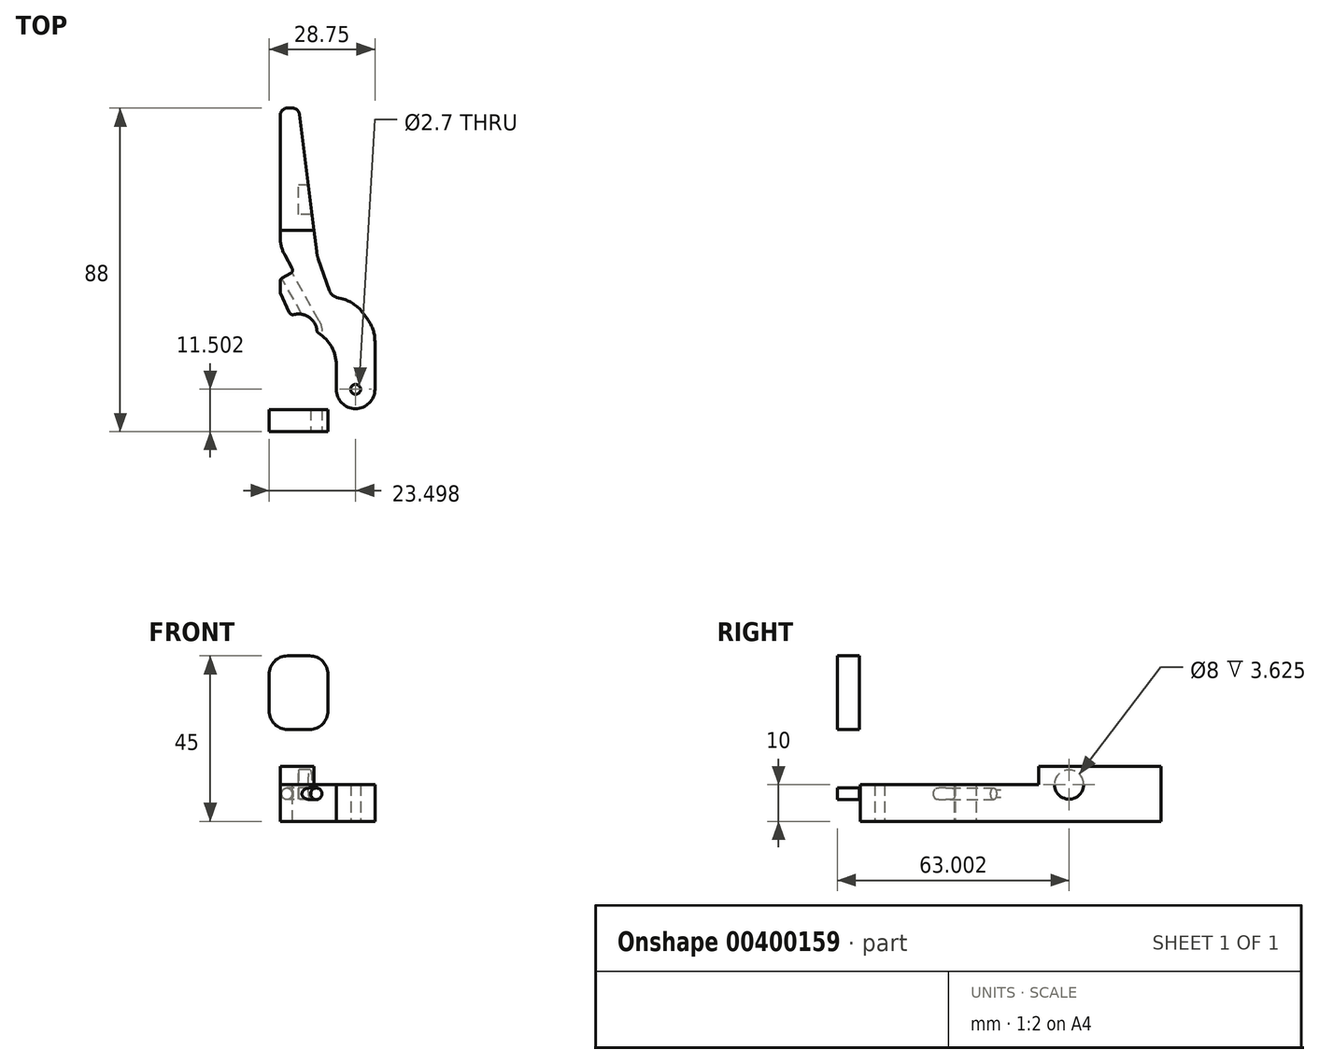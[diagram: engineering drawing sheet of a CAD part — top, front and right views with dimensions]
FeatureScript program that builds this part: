
annotation { "Feature Type Name" : "Feature", "Feature Type Description" : "" }
export const myFeature = defineFeature(function(context is Context, id is Id, definition is map)
    precondition{}
    {
        {
            var Q0;
            Q0=qCreatedBy(makeId("Top.planeOp"),FACE);
            var sketch = newSketch(context, id + "F0", { "sketchPlane" : qUnion([Q0])});
            skLineSegment(sketch, "E0", {"start": v(-10.82, 50.62) * mm, "end": v(-10.82, 5.62) * mm});
            skCircle(sketch, "E1.MirrorC", {"center": v(-0.32, 45.12) * mm, "radius": 1.75 * mm});
            skCircle(sketch, "E2.MirrorC", {"center": v(-0.32, 14.12) * mm, "radius": 1.75 * mm});
            skCircle(sketch, "E3.MirrorC", {"center": v(30.68, 45.12) * mm, "radius": 1.75 * mm});
            skLineSegment(sketch, "E4.MirrorCS", {"start": v(46.18, 90.62) * mm, "end": v(41.18, 90.62) * mm});
            skLineSegment(sketch, "E5.MirrorCS", {"start": v(41.18, 90.62) * mm, "end": v(36.18, 50.62) * mm});
            skLineSegment(sketch, "E6.MirrorCS", {"start": v(36.18, 50.62) * mm, "end": v(30.68, 50.62) * mm});
            skLineSegment(sketch, "E7.MirrorCS", {"start": v(36.18, 8.62) * mm, "end": v(-5.82, 8.62) * mm});
            skLineSegment(sketch, "E8.MirrorCS", {"start": v(36.18, 50.62) * mm, "end": v(36.18, 8.62) * mm});
            skLineSegment(sketch, "E9.MirrorCS", {"start": v(-5.82, 50.62) * mm, "end": v(-5.82, 8.62) * mm});
            skArc(sketch, "E10.MirrorC", {"start": v(-0.32, 50.62) * mm, "mid": v(3.57, 49.01) * mm, "end": v(5.18, 45.12) * mm});
            skLineSegment(sketch, "E11.MirrorCS", {"start": v(46.18, 5.62) * mm, "end": v(46.18, 90.62) * mm});
            skLineSegment(sketch, "E12.MirrorCS", {"start": v(-10.82, 5.62) * mm, "end": v(46.18, 5.62) * mm});
            skLineSegment(sketch, "E13", {"start": v(-5.82, 50.62) * mm, "end": v(-10.82, 50.62) * mm});
            skLineSegment(sketch, "E14", {"start": v(5.18, 45.12) * mm, "end": v(5.18, 35.3) * mm});
            skLineSegment(sketch, "E15", {"start": v(-5.82, 8.62) * mm, "end": v(-5.82, 5.62) * mm});
            skLineSegment(sketch, "E16", {"start": v(36.18, 8.62) * mm, "end": v(36.18, 5.62) * mm});
            skArc(sketch, "E17", {"start": v(5.18, 35.3) * mm, "mid": v(3.68, 29.62) * mm, "end": v(5.18, 23.94) * mm});
            skArc(sketch, "E18", {"start": v(5.18, 23.94) * mm, "mid": v(9.4, 19.68) * mm, "end": v(15.18, 18.12) * mm});
            skLineSegment(sketch, "E19", {"start": v(15.18, 18.12) * mm, "end": v(23.18, 18.12) * mm});
            skPoint(sketch, "E20.end.orphan", {"position": v(15.18, 8.62) * mm});
            skLineSegment(sketch, "E21", {"start": v(23.18, 18.12) * mm, "end": v(23.18, 8.62) * mm});
            skPoint(sketch, "E22.trimOffspring.end.orphan", {"position": v(23.18, 0) * mm});
            skCircle(sketch, "E23", {"center": v(30.68, 14.12) * mm, "radius": 1.35 * mm});
            skLineSegment(sketch, "E24.trimOffspring", {"start": v(-0.32, 50.62) * mm, "end": v(-5.82, 50.62) * mm});
            skLineSegment(sketch, "E25", {"start": v(10.18, 65.16) * mm, "end": v(10.18, 52.87) * mm});
            skLineSegment(sketch, "E26", {"start": v(10.18, 65.16) * mm, "end": v(10.18, 90.62) * mm});
            skLineSegment(sketch, "E27", {"start": v(10.18, 90.62) * mm, "end": v(15.18, 90.62) * mm});
            skLineSegment(sketch, "E28", {"start": v(15.18, 90.62) * mm, "end": v(20.18, 50.62) * mm});
            skCircle(sketch, "E29", {"center": v(15.18, 29.62) * mm, "radius": 4 * mm});
            skArc(sketch, "E30", {"start": v(30.68, 50.62) * mm, "mid": v(25.18, 45.12) * mm, "end": v(30.68, 39.62) * mm});
            skLineSegment(sketch, "E31", {"start": v(30.68, 39.62) * mm, "end": v(36.18, 39.62) * mm});
            skLineSegment(sketch, "E32", {"start": v(10.18, 42.2) * mm, "end": v(10.18, 40.62) * mm});
            skLineSegment(sketch, "E33", {"start": v(27.5, 38.6) * mm, "end": v(30.68, 37.71) * mm});
            skLineSegment(sketch, "E34", {"start": v(10.18, 40.35) * mm, "end": v(12.75, 34.83) * mm});
            skLineSegment(sketch, "E35", {"start": v(10.18, 40.62) * mm, "end": v(10.18, 40.35) * mm});
            skArc(sketch, "E36", {"start": v(25.43, 14.12) * mm, "mid": v(30.68, 8.87) * mm, "end": v(35.93, 14.12) * mm});
            skLineSegment(sketch, "E37", {"start": v(25.43, 14.12) * mm, "end": v(25.43, 29.62) * mm});
            skLineSegment(sketch, "E38", {"start": v(35.93, 14.12) * mm, "end": v(35.93, 30.4) * mm});
            skLineSegment(sketch, "E39", {"start": v(30.68, 37.71) * mm, "end": v(35.93, 30.4) * mm});
            skLineSegment(sketch, "E40", {"start": v(11.37, 37.8) * mm, "end": v(9.16, 36.55) * mm});
            skPoint(sketch, "E41", {"position": v(12.24, 44.65) * mm});
            skLineSegment(sketch, "E42.trimOffspring", {"start": v(14.96, 39.81) * mm, "end": v(19.36, 31.97) * mm});
            skArc(sketch, "E43", {"start": v(19.98, 29.62) * mm, "mid": v(19.82, 30.84) * mm, "end": v(19.36, 31.97) * mm});
            skArc(sketch, "E44", {"start": v(20.18, 29.62) * mm, "mid": v(17.87, 33.84) * mm, "end": v(13.07, 34.15) * mm});
            skLineSegment(sketch, "E45", {"start": v(25.43, 29.62) * mm, "end": v(20.18, 29.62) * mm});
            skLineSegment(sketch, "E46", {"start": v(12.75, 34.83) * mm, "end": v(13.07, 34.15) * mm});
            skLineSegment(sketch, "E47.trimOffspring", {"start": v(10.18, 44.1) * mm, "end": v(10.18, 42.2) * mm});
            skLineSegment(sketch, "E48", {"start": v(10.18, 44.1) * mm, "end": v(13.93, 46.2) * mm});
            skLineSegment(sketch, "E49", {"start": v(13.93, 46.2) * mm, "end": v(10.18, 52.87) * mm});
            skPoint(sketch, "E50.start.orphan", {"position": v(12.24, 45.94) * mm});
            skLineSegment(sketch, "E51", {"start": v(27.5, 38.6) * mm, "end": v(25.54, 39.13) * mm});
            skLineSegment(sketch, "E52", {"start": v(20.18, 50.62) * mm, "end": v(23.51, 41.04) * mm});
            skPoint(sketch, "E53.visualSharp", {"position": v(24.03, 39.55) * mm});
            skArc(sketch, "E53.filletArc", {"start": v(23.51, 41.04) * mm, "mid": v(24.3, 39.84) * mm, "end": v(25.54, 39.13) * mm});
            skLineSegment(sketch, "E54", {"start": v(10.18, 57.39) * mm, "end": v(19.33, 57.39) * mm});
            skSolve(sketch);
        }
        {
            var Q0;
            Q0=makeQuery(id+"F0.imprint","IMPRINT",FACE,{"disambiguationData":[TD([[makeQuery(id+"F0.imprint","IMPRINT",EDGE,{"derivedFrom":sQuery(id+"F0.wireOp",EDGE,"E1.MirrorC")}),1.0]])]});
            var Q1;
            Q1=makeQuery(id+"F0.imprint","IMPRINT",FACE,{"disambiguationData":[TD([[makeQuery(id+"F0.imprint","IMPRINT",EDGE,{"derivedFrom":sQuery(id+"F0.wireOp",EDGE,"E3.MirrorC")}),1.0]])]});
            var Q2;
            Q2=makeQuery(id+"F0.imprint","IMPRINT",FACE,{"disambiguationData":[TD([[makeQuery(id+"F0.imprint","IMPRINT",EDGE,{"derivedFrom":sQuery(id+"F0.wireOp",EDGE,"E0")}),1.0]])]});
            var Q3;
            Q3=makeQuery(id+"F0.imprint","IMPRINT",FACE,{"disambiguationData":[TD([[makeQuery(id+"F0.imprint","IMPRINT",EDGE,{"derivedFrom":sQuery(id+"F0.wireOp",EDGE,"E4.MirrorCS")}),1.0]])]});
            var Q4;
            {var subQ0=sQuery(id+"F0.wireOp",EDGE,"E15");Q4=makeQuery(id+"F0.imprint","IMPRINT",FACE,{"disambiguationData":[TD([[makeQuery(id+"F0.imprint","IMPRINT",EDGE,{"derivedFrom":subQ0}),1.0]])]});}
            extrude(context, id + "F1", {"entities" : qUnion([Q0, Q1, Q2, Q3, Q4]), "depth" : 5 * mm});
        }
        {
            var Q0;
            {var subQ1=sQuery(id+"F0.wireOp",EDGE,"E0");Q0=makeQuery(id+"F0.imprint","IMPRINT",FACE,{"disambiguationData":[TD([[makeQuery(id+"F0.imprint","IMPRINT",EDGE,{"derivedFrom":subQ1}),1.0]])]});}
            var Q1;
            {var subQ0=sQuery(id+"F0.wireOp",EDGE,"E15");Q1=makeQuery(id+"F0.imprint","IMPRINT",FACE,{"disambiguationData":[TD([[makeQuery(id+"F0.imprint","IMPRINT",EDGE,{"derivedFrom":subQ0}),1.0]])]});}
            var Q2;
            Q2=makeQuery(id+"F0.imprint","IMPRINT",FACE,{"disambiguationData":[TD([[makeQuery(id+"F0.imprint","IMPRINT",EDGE,{"derivedFrom":sQuery(id+"F0.wireOp",EDGE,"E4.MirrorCS")}),1.0]])]});
            extrude(context, id + "F2", {"entities" : qUnion([Q0, Q1, Q2]), "operationType" : NewBodyOperationType.ADD, "depth" : 10 * mm});
        }
        {
            var Q0;
            {var subQ0=sQuery(id+"F0.wireOp",EDGE,"E15");Q0=makeQuery(id+"F0.imprint","IMPRINT",FACE,{"disambiguationData":[TD([[makeQuery(id+"F0.imprint","IMPRINT",EDGE,{"derivedFrom":subQ0}),1.0]])]});}
            extrude(context, id + "F3", {"entities" : qUnion([Q0]), "operationType" : NewBodyOperationType.ADD, "depth" : 20 * mm});
        }
        {
            var Q0;
            Q0=makeQuery(id+"F3.opExtrude","CAP_FACE",FACE,{"disambiguationData":[OSD([sQuery(id+"F0.wireOp",EDGE,"E7.MirrorCS"),sQuery(id+"F0.wireOp",EDGE,"E12.MirrorCS"),sQuery(id+"F0.wireOp",EDGE,"E15"),sQuery(id+"F0.wireOp",EDGE,"E16")])],"isStart":false});
            var sketch = newSketch(context, id + "F4", { "sketchPlane" : qUnion([Q0])});
            skLineSegment(sketch, "E55.bottom", {"start": v(7.18, 8.62) * mm, "end": v(23.18, 8.62) * mm});
            skLineSegment(sketch, "E55.top", {"start": v(7.18, 5.62) * mm, "end": v(23.18, 5.62) * mm});
            skLineSegment(sketch, "E55.left", {"start": v(7.18, 8.62) * mm, "end": v(7.18, 5.62) * mm});
            skLineSegment(sketch, "E55.right", {"start": v(23.18, 8.62) * mm, "end": v(23.18, 5.62) * mm});
            skSolve(sketch);
        }
        {
            var Q0;
            Q0=makeQuery(id+"F2.opExtrude","SWEPT_EDGE",EDGE,{"disambiguationData":[OSD([sQuery(id+"F0.wireOp",EDGE,"E7.MirrorCS"),sQuery(id+"F0.wireOp",EDGE,"E9.MirrorCS"),sQuery(id+"F0.wireOp",EDGE,"E15")])]});
            var Q1;
            Q1=makeQuery(id+"F2.opExtrude","SWEPT_EDGE",EDGE,{"disambiguationData":[OSD([sQuery(id+"F0.wireOp",EDGE,"E7.MirrorCS"),sQuery(id+"F0.wireOp",EDGE,"E8.MirrorCS"),sQuery(id+"F0.wireOp",EDGE,"E16")])]});
            chamfer(context, id + "F5", {"entities" : qUnion([Q0, Q1]), "width" : 3.5 * mm, "tangentPropagation" : true});
        }
        {
            var Q0;
            {var subQ0=sQuery(id+"F0.wireOp",EDGE,"E11.MirrorCS");Q0=makeQuery(id+"F2.boolean.opBoolean","MERGE",FACE,{"derivedFrom":[makeQuery(id+"F1.opExtrude","SWEPT_FACE",FACE,{"disambiguationData":[OSD([subQ0])]}),makeQuery(id+"F2.opExtrude","SWEPT_FACE",FACE,{"disambiguationData":[OSD([subQ0])]})]});}
            var sketch = newSketch(context, id + "F6", { "sketchPlane" : qUnion([Q0])});
            skCircle(sketch, "E56", {"center": v(65.62, 5) * mm, "radius": 4 * mm});
            skCircle(sketch, "E57.cCircle", {"center": v(65.62, 5) * mm, "radius": 2.75 * mm, "construction": true});
            skLineSegment(sketch, "E57.0", {"start": v(62.87, 3.41) * mm, "end": v(62.87, 6.59) * mm});
            skLineSegment(sketch, "E57.1", {"start": v(62.87, 6.59) * mm, "end": v(65.62, 8.18) * mm});
            skLineSegment(sketch, "E57.2", {"start": v(65.62, 8.18) * mm, "end": v(68.37, 6.59) * mm});
            skLineSegment(sketch, "E57.3", {"start": v(68.37, 6.59) * mm, "end": v(68.37, 3.41) * mm});
            skLineSegment(sketch, "E57.4", {"start": v(68.37, 3.41) * mm, "end": v(65.62, 1.82) * mm});
            skLineSegment(sketch, "E57.5", {"start": v(65.62, 1.82) * mm, "end": v(62.87, 3.41) * mm});
            skPoint(sketch, "E57.0.midPoint", {"position": v(62.87, 5) * mm});
            skCircle(sketch, "E58", {"center": v(65.62, 5) * mm, "radius": 1.6 * mm});
            skSolve(sketch);
        }
        {
            var Q0;
            Q0=makeQuery(id+"F6.imprint","IMPRINT",FACE,{"disambiguationData":[TD([[makeQuery(id+"F6.imprint","IMPRINT",EDGE,{"derivedFrom":sQuery(id+"F6.wireOp",EDGE,"E56")}),1.0]])]});
            extrude(context, id + "F7", {"entities" : qUnion([Q0]), "operationType" : NewBodyOperationType.REMOVE, "oppositeDirection" : true, "depth" : 25 * mm});
        }
        {
            var Q0;
            Q0=makeQuery(id+"F6.imprint","IMPRINT",FACE,{"disambiguationData":[TD([[makeQuery(id+"F6.imprint","IMPRINT",EDGE,{"derivedFrom":sQuery(id+"F6.wireOp",EDGE,"E56")}),1.0]])]});
            extrude(context, id + "F8", {"entities" : qUnion([Q0]), "operationType" : NewBodyOperationType.ADD, "oppositeDirection" : true, "depth" : 6.5 * mm});
        }
        {
            var Q0;
            Q0=makeQuery(id+"F6.imprint","IMPRINT",FACE,{"disambiguationData":[TD([[makeQuery(id+"F6.imprint","IMPRINT",EDGE,{"derivedFrom":sQuery(id+"F6.wireOp",EDGE,"E57.0")}),-1.0]])]});
            extrude(context, id + "F9", {"entities" : qUnion([Q0]), "operationType" : NewBodyOperationType.REMOVE, "oppositeDirection" : true, "depth" : 25 * mm});
        }
        {
            var Q0;
            Q0=makeQuery(id+"F6.imprint","IMPRINT",FACE,{"disambiguationData":[TD([[makeQuery(id+"F6.imprint","IMPRINT",EDGE,{"derivedFrom":sQuery(id+"F6.wireOp",EDGE,"E57.0")}),-1.0]])]});
            extrude(context, id + "F10", {"entities" : qUnion([Q0]), "operationType" : NewBodyOperationType.ADD, "oppositeDirection" : true, "depth" : 4 * mm});
        }
        {
            var Q0;
            Q0=makeQuery(id+"F6.imprint","IMPRINT",FACE,{"disambiguationData":[TD([[makeQuery(id+"F6.imprint","IMPRINT",EDGE,{"derivedFrom":sQuery(id+"F6.wireOp",EDGE,"E58")}),1.0]])]});
            extrude(context, id + "F11", {"entities" : qUnion([Q0]), "operationType" : NewBodyOperationType.REMOVE, "oppositeDirection" : true, "depth" : 25 * mm});
        }
        {
            var Q0;
            {var subQ0=sQuery(id+"F0.wireOp",EDGE,"E12.MirrorCS");Q0=makeQuery(id+"F16.boolean.opBoolean","MERGE",FACE,{"derivedFrom":[makeQuery(id+"F3.boolean.opBoolean","MERGE",FACE,{"derivedFrom":[makeQuery(id+"F2.boolean.opBoolean","MERGE",FACE,{"derivedFrom":[makeQuery(id+"F1.opExtrude","SWEPT_FACE",FACE,{"disambiguationData":[OSD([subQ0])]}),makeQuery(id+"F2.opExtrude","SWEPT_FACE",FACE,{"disambiguationData":[OSD([subQ0])]})]}),makeQuery(id+"F3.opExtrude","SWEPT_FACE",FACE,{"disambiguationData":[OSD([subQ0])]})]}),makeQuery(id+"F16.opExtrude","SWEPT_FACE",FACE,{"disambiguationData":[OSD([sQuery(id+"F4.wireOp",EDGE,"E55.top")])]})]});}
            var sketch = newSketch(context, id + "F12", { "sketchPlane" : qUnion([Q0])});
            skLineSegment(sketch, "E59", {"start": v(-10.82, 2.5) * mm, "end": v(46.18, 2.5) * mm});
            skCircle(sketch, "E60", {"center": v(19.98, 2.5) * mm, "radius": 1.55 * mm});
            skSolve(sketch);
        }
        {
            var Q0;
            {var subQ0=sQuery(id+"F12.wireOp",EDGE,"E60");var subQ1=sQuery(id+"F12.wireOp",EDGE,"E59");var subQ2=makeQuery(id+"F12.imprint","INTERSECT",VERTEX,{"disambiguationData":[OD(0.0)],"derivedFrom":[subQ1,subQ0]});Q0=makeQuery(id+"F12.imprint","IMPRINT",FACE,{"disambiguationData":[TD([[makeQuery(id+"F12.imprint","IMPRINT",EDGE,{"disambiguationData":[TD([[subQ2,-1.0]])],"derivedFrom":subQ1}),1.0]])]});}
            var Q1;
            {var subQ0=sQuery(id+"F12.wireOp",EDGE,"E60");var subQ1=sQuery(id+"F12.wireOp",EDGE,"E59");var subQ2=makeQuery(id+"F12.imprint","INTERSECT",VERTEX,{"disambiguationData":[OD(0.0)],"derivedFrom":[subQ1,subQ0]});Q1=makeQuery(id+"F12.imprint","IMPRINT",FACE,{"disambiguationData":[TD([[makeQuery(id+"F12.imprint","IMPRINT",EDGE,{"disambiguationData":[TD([[subQ2,-1.0]])],"derivedFrom":subQ1}),-1.0]])]});}
            extrude(context, id + "F13", {"entities" : qUnion([Q0, Q1]), "operationType" : NewBodyOperationType.REMOVE, "endBound" : BoundingType.THROUGH_ALL, "oppositeDirection" : true, "depth" : 25 * mm});
        }
        {
            var Q0;
            Q0=makeQuery(id+"F0.imprint","IMPRINT",FACE,{"disambiguationData":[TD([[makeQuery(id+"F0.imprint","IMPRINT",EDGE,{"derivedFrom":sQuery(id+"F0.wireOp",EDGE,"E23")}),-1.0]])]});
            var Q1;
            Q1=makeQuery(id+"F0.imprint","IMPRINT",FACE,{"disambiguationData":[TD([[makeQuery(id+"F0.imprint","IMPRINT",EDGE,{"derivedFrom":sQuery(id+"F0.wireOp",EDGE,"E25")}),1.0]])]});
            extrude(context, id + "F14", {"entities" : qUnion([Q0, Q1]), "depth" : 5 * mm});
        }
        {
            var Q0;
            Q0=makeQuery(id+"F14.opExtrude","SWEPT_FACE",FACE,{"disambiguationData":[OSD([sQuery(id+"F0.wireOp",EDGE,"E45")])]});
            var sketch = newSketch(context, id + "F15", { "sketchPlane" : qUnion([Q0])});
            skCircle(sketch, "E61", {"center": v(19.98, 2.5) * mm, "radius": 1.6 * mm});
            skSolve(sketch);
        }
        {
            var Q0;
            Q0=makeQuery(id+"F4.imprint","IMPRINT",FACE,{"disambiguationData":[TD([[makeQuery(id+"F4.imprint","IMPRINT",EDGE,{"derivedFrom":sQuery(id+"F4.wireOp",EDGE,"E55.bottom")}),1.0]])]});
            extrude(context, id + "F16", {"entities" : qUnion([Q0]), "operationType" : NewBodyOperationType.ADD, "depth" : 20 * mm});
        }
        {
            var Q0;
            {var subQ0=sQuery(id+"F15.wireOp",EDGE,"E61");var subQ1=makeQuery(id+"F14.opExtrude","SWEPT_EDGE",EDGE,{"disambiguationData":[OSD([sQuery(id+"F0.wireOp",EDGE,"E44"),sQuery(id+"F0.wireOp",EDGE,"E45")])]});var subQ2=makeQuery(id+"F15.imprint","INTERSECT",VERTEX,{"disambiguationData":[OD(0.0)],"derivedFrom":[subQ1,subQ0]});Q0=makeQuery(id+"F15.imprint","IMPRINT",FACE,{"disambiguationData":[TD([[makeQuery(id+"F15.imprint","IMPRINT",EDGE,{"disambiguationData":[TD([[subQ2,-1.0]])],"derivedFrom":subQ0}),1.0]])]});}
            var Q1;
            {var subQ0=sQuery(id+"F15.wireOp",EDGE,"E61");var subQ1=makeQuery(id+"F14.opExtrude","SWEPT_EDGE",EDGE,{"disambiguationData":[OSD([sQuery(id+"F0.wireOp",EDGE,"E44"),sQuery(id+"F0.wireOp",EDGE,"E45")])]});var subQ2=makeQuery(id+"F15.imprint","INTERSECT",VERTEX,{"disambiguationData":[OD(0.0)],"derivedFrom":[subQ1,subQ0]});Q1=makeQuery(id+"F15.imprint","IMPRINT",FACE,{"disambiguationData":[TD([[makeQuery(id+"F15.imprint","IMPRINT",EDGE,{"disambiguationData":[TD([[subQ2,1.0]])],"derivedFrom":subQ0}),1.0]])]});}
            var Q2;
            Q2=sQuery(id+"F0.wireOp",EDGE,"E43");
            var Q3;
            Q3=sQuery(id+"F0.wireOp",EDGE,"E42.trimOffspring");
            sweep(context, id + "F17", {"operationType" : NewBodyOperationType.REMOVE, "profiles" : qUnion([Q0, Q1]), "path" : qUnion([Q2, Q3])});
        }
        {
            var Q0;
            Q0=sQuery(id+"F0.wireOp",EDGE,"E40");
            cPlane(context, id + "F18", {"entities" : qUnion([Q0]), "cplaneType" : CPlaneType.LINE_ANGLE, "offset" : 25 * mm, "angle" : 0 * degree, "width" : 150 * mm, "height" : 150 * mm});
        }
        {
            var Q0;
            Q0=qCreatedBy(id+"F18.planeOp",FACE);
            var sketch = newSketch(context, id + "F19", { "sketchPlane" : qUnion([Q0])});
            skCircle(sketch, "E62", {"center": v(32.55, 2.5) * mm, "radius": 1.6 * mm});
            skSolve(sketch);
        }
        {
            var Q0;
            Q0 = qSketchRegion(id + "F19", true);
            extrude(context, id + "F20", {"entities" : qUnion([Q0]), "operationType" : NewBodyOperationType.REMOVE, "oppositeDirection" : true, "depth" : 25 * mm});
        }
        {
            var Q0;
            Q0=makeQuery(id+"F0.imprint","IMPRINT",FACE,{"disambiguationData":[TD([[makeQuery(id+"F0.imprint","IMPRINT",EDGE,{"derivedFrom":sQuery(id+"F0.wireOp",EDGE,"E25")}),1.0]])]});
            extrude(context, id + "F21", {"entities" : qUnion([Q0]), "operationType" : NewBodyOperationType.ADD, "depth" : 10 * mm});
        }
        {
            var Q0;
            Q0=makeQuery(id+"F14.opExtrude","SWEPT_EDGE",EDGE,{"disambiguationData":[OSD([sQuery(id+"F0.wireOp",EDGE,"E47.trimOffspring"),sQuery(id+"F0.wireOp",EDGE,"E48")])]});
            var Q1;
            Q1=makeQuery(id+"F14.opExtrude","SWEPT_EDGE",EDGE,{"disambiguationData":[OSD([sQuery(id+"F0.wireOp",EDGE,"E48"),sQuery(id+"F0.wireOp",EDGE,"E49")])]});
            fillet(context, id + "F22", {"entities" : qUnion([Q0, Q1]), "radius" : 1 * mm, "tangentPropagation" : true, "allowEdgeOverflow" : false});
        }
        {
            var Q0;
            Q0=makeQuery(id+"F14.opExtrude","CAP_FACE",FACE,{"disambiguationData":[OSD([sQuery(id+"F0.wireOp",EDGE,"E23"),sQuery(id+"F0.wireOp",EDGE,"E25"),sQuery(id+"F0.wireOp",EDGE,"E26"),sQuery(id+"F0.wireOp",EDGE,"E27"),sQuery(id+"F0.wireOp",EDGE,"E28"),sQuery(id+"F0.wireOp",EDGE,"E32"),sQuery(id+"F0.wireOp",EDGE,"E33"),sQuery(id+"F0.wireOp",EDGE,"E34"),sQuery(id+"F0.wireOp",EDGE,"E35"),sQuery(id+"F0.wireOp",EDGE,"E36"),sQuery(id+"F0.wireOp",EDGE,"E37"),sQuery(id+"F0.wireOp",EDGE,"E38"),sQuery(id+"F0.wireOp",EDGE,"E39"),sQuery(id+"F0.wireOp",EDGE,"E44"),sQuery(id+"F0.wireOp",EDGE,"E45"),sQuery(id+"F0.wireOp",EDGE,"E46"),sQuery(id+"F0.wireOp",EDGE,"E47.trimOffspring"),sQuery(id+"F0.wireOp",EDGE,"E48"),sQuery(id+"F0.wireOp",EDGE,"E49"),sQuery(id+"F0.wireOp",EDGE,"E51"),sQuery(id+"F0.wireOp",EDGE,"E52"),sQuery(id+"F0.wireOp",EDGE,"E53.filletArc")])],"isStart":true});
            extrude(context, id + "F23", {"entities" : qUnion([Q0]), "operationType" : NewBodyOperationType.ADD, "depth" : 5 * mm});
        }
        {
            var Q0;
            {var subQ0=sQuery(id+"F0.wireOp",EDGE,"E39");var subQ1=sQuery(id+"F0.wireOp",EDGE,"E33");Q0=makeQuery(id+"F23.boolean.opBoolean","MERGE",EDGE,{"derivedFrom":[makeQuery(id+"F14.opExtrude","SWEPT_EDGE",EDGE,{"disambiguationData":[OSD([subQ1,subQ0])]}),makeQuery(id+"F23.opExtrude","SWEPT_EDGE",EDGE,{"disambiguationData":[OSD([subQ1,subQ0])]})]});}
            var Q1;
            {var subQ0=sQuery(id+"F0.wireOp",EDGE,"E39");var subQ1=sQuery(id+"F0.wireOp",EDGE,"E38");Q1=makeQuery(id+"F23.boolean.opBoolean","MERGE",EDGE,{"derivedFrom":[makeQuery(id+"F14.opExtrude","SWEPT_EDGE",EDGE,{"disambiguationData":[OSD([subQ1,subQ0])]}),makeQuery(id+"F23.opExtrude","SWEPT_EDGE",EDGE,{"disambiguationData":[OSD([subQ1,subQ0])]})]});}
            var Q2;
            {var subQ0=sQuery(id+"F0.wireOp",EDGE,"E45");var subQ1=sQuery(id+"F0.wireOp",EDGE,"E37");Q2=makeQuery(id+"F23.boolean.opBoolean","MERGE",EDGE,{"derivedFrom":[makeQuery(id+"F14.opExtrude","SWEPT_EDGE",EDGE,{"disambiguationData":[OSD([subQ1,subQ0])]}),makeQuery(id+"F23.opExtrude","SWEPT_EDGE",EDGE,{"disambiguationData":[OSD([subQ1,subQ0])]})]});}
            var Q3;
            {var subQ0=sQuery(id+"F0.wireOp",EDGE,"E49");var subQ1=sQuery(id+"F0.wireOp",EDGE,"E25");Q3=makeQuery(id+"F23.boolean.opBoolean","MERGE",EDGE,{"derivedFrom":[makeQuery(id+"F14.opExtrude","SWEPT_EDGE",EDGE,{"disambiguationData":[OSD([subQ1,subQ0])]}),makeQuery(id+"F23.opExtrude","SWEPT_EDGE",EDGE,{"disambiguationData":[OSD([subQ1,subQ0])]})]});}
            var Q4;
            {var subQ0=sQuery(id+"F0.wireOp",EDGE,"E52");var subQ1=sQuery(id+"F0.wireOp",EDGE,"E28");Q4=makeQuery(id+"F23.boolean.opBoolean","MERGE",EDGE,{"derivedFrom":[makeQuery(id+"F14.opExtrude","SWEPT_EDGE",EDGE,{"disambiguationData":[OSD([subQ1,subQ0])]}),makeQuery(id+"F23.opExtrude","SWEPT_EDGE",EDGE,{"disambiguationData":[OSD([subQ1,subQ0])]})]});}
            fillet(context, id + "F24", {"entities" : qUnion([Q0, Q1, Q2, Q3, Q4]), "radius" : 10 * mm, "tangentPropagation" : true, "allowEdgeOverflow" : false});
        }
        {
            var Q0;
            {var subQ0=sQuery(id+"F0.wireOp",EDGE,"E26");var subQ1=sQuery(id+"F0.wireOp",EDGE,"E25");Q0=makeQuery(id+"F23.boolean.opBoolean","MERGE",FACE,{"derivedFrom":[makeQuery(id+"F21.boolean.opBoolean","MERGE",FACE,{"derivedFrom":[makeQuery(id+"F14.opExtrude","SWEPT_FACE",FACE,{"disambiguationData":[OSD([subQ1,subQ0])]}),makeQuery(id+"F21.opExtrude","SWEPT_FACE",FACE,{"disambiguationData":[OSD([subQ1,subQ0])]})]}),makeQuery(id+"F23.opExtrude","SWEPT_FACE",FACE,{"disambiguationData":[OSD([subQ1,subQ0])]})]});}
            var sketch = newSketch(context, id + "F25", { "sketchPlane" : qUnion([Q0])});
            skCircle(sketch, "E63", {"center": v(-65.62, 5) * mm, "radius": 4 * mm});
            skSolve(sketch);
        }
        {
            var Q0;
            Q0 = qSketchRegion(id + "F25", true);
            extrude(context, id + "F26", {"entities" : qUnion([Q0]), "operationType" : NewBodyOperationType.REMOVE, "oppositeDirection" : true, "depth" : 13.3 * mm});
        }
        {
            var Q0;
            Q0=makeQuery(id+"F25.imprint","IMPRINT",FACE,{"disambiguationData":[TD([[makeQuery(id+"F25.imprint","IMPRINT",EDGE,{"derivedFrom":sQuery(id+"F25.wireOp",EDGE,"E63")}),1.0]])]});
            extrude(context, id + "F27", {"entities" : qUnion([Q0]), "operationType" : NewBodyOperationType.ADD, "oppositeDirection" : true, "depth" : 5 * mm});
        }
        {
            var Q0;
            Q0=makeQuery(id+"F16.opExtrude","CAP_EDGE",EDGE,{"disambiguationData":[OSD([sQuery(id+"F4.wireOp",EDGE,"E55.left")])],"isStart":true});
            var Q1;
            Q1=makeQuery(id+"F16.opExtrude","CAP_EDGE",EDGE,{"disambiguationData":[OSD([sQuery(id+"F4.wireOp",EDGE,"E55.right")])],"isStart":true});
            var Q2;
            Q2=makeQuery(id+"F3.boolean.opBoolean","INTERSECT",EDGE,{"derivedFrom":[makeQuery(id+"F2.opExtrude","CAP_FACE",FACE,{"disambiguationData":[OSD([sQuery(id+"F0.wireOp",EDGE,"E0"),sQuery(id+"F0.wireOp",EDGE,"E4.MirrorCS"),sQuery(id+"F0.wireOp",EDGE,"E5.MirrorCS"),sQuery(id+"F0.wireOp",EDGE,"E7.MirrorCS"),sQuery(id+"F0.wireOp",EDGE,"E8.MirrorCS"),sQuery(id+"F0.wireOp",EDGE,"E9.MirrorCS"),sQuery(id+"F0.wireOp",EDGE,"E11.MirrorCS"),sQuery(id+"F0.wireOp",EDGE,"E12.MirrorCS"),sQuery(id+"F0.wireOp",EDGE,"E13")])],"isStart":false}),makeQuery(id+"F3.opExtrude","SWEPT_FACE",FACE,{"disambiguationData":[OSD([sQuery(id+"F0.wireOp",EDGE,"E16")])]})]});
            var Q3;
            Q3=makeQuery(id+"F16.opExtrude","CAP_EDGE",EDGE,{"disambiguationData":[OSD([sQuery(id+"F4.wireOp",EDGE,"E55.right")])],"isStart":false});
            var Q4;
            Q4=makeQuery(id+"F16.opExtrude","CAP_EDGE",EDGE,{"disambiguationData":[OSD([sQuery(id+"F4.wireOp",EDGE,"E55.left")])],"isStart":false});
            var Q5;
            {var subQ0=sQuery(id+"F0.wireOp",EDGE,"E13");var subQ1=sQuery(id+"F0.wireOp",EDGE,"E0");Q5=makeQuery(id+"F2.boolean.opBoolean","MERGE",EDGE,{"derivedFrom":[makeQuery(id+"F1.opExtrude","SWEPT_EDGE",EDGE,{"disambiguationData":[OSD([subQ1,subQ0])]}),makeQuery(id+"F2.opExtrude","SWEPT_EDGE",EDGE,{"disambiguationData":[OSD([subQ1,subQ0])]})]});}
            fillet(context, id + "F28", {"entities" : qUnion([Q0, Q1, Q2, Q3, Q4, Q5]), "radius" : 5 * mm, "tangentPropagation" : true, "allowEdgeOverflow" : false});
        }
        {
            var Q0;
            {var subQ0=sQuery(id+"F0.wireOp",EDGE,"E27");var subQ1=sQuery(id+"F0.wireOp",EDGE,"E26");Q0=makeQuery(id+"F23.boolean.opBoolean","MERGE",EDGE,{"derivedFrom":[makeQuery(id+"F21.boolean.opBoolean","MERGE",EDGE,{"derivedFrom":[makeQuery(id+"F14.opExtrude","SWEPT_EDGE",EDGE,{"disambiguationData":[OSD([subQ1,subQ0])]}),makeQuery(id+"F21.opExtrude","SWEPT_EDGE",EDGE,{"disambiguationData":[OSD([subQ1,subQ0])]})]}),makeQuery(id+"F23.opExtrude","SWEPT_EDGE",EDGE,{"disambiguationData":[OSD([subQ1,subQ0])]})]});}
            var Q1;
            {var subQ0=sQuery(id+"F0.wireOp",EDGE,"E28");var subQ1=sQuery(id+"F0.wireOp",EDGE,"E27");Q1=makeQuery(id+"F23.boolean.opBoolean","MERGE",EDGE,{"derivedFrom":[makeQuery(id+"F21.boolean.opBoolean","MERGE",EDGE,{"derivedFrom":[makeQuery(id+"F14.opExtrude","SWEPT_EDGE",EDGE,{"disambiguationData":[OSD([subQ1,subQ0])]}),makeQuery(id+"F21.opExtrude","SWEPT_EDGE",EDGE,{"disambiguationData":[OSD([subQ1,subQ0])]})]}),makeQuery(id+"F23.opExtrude","SWEPT_EDGE",EDGE,{"disambiguationData":[OSD([subQ1,subQ0])]})]});}
            var Q2;
            {var subQ0=sQuery(id+"F0.wireOp",EDGE,"E5.MirrorCS");var subQ1=sQuery(id+"F0.wireOp",EDGE,"E4.MirrorCS");Q2=makeQuery(id+"F2.boolean.opBoolean","MERGE",EDGE,{"derivedFrom":[makeQuery(id+"F1.opExtrude","SWEPT_EDGE",EDGE,{"disambiguationData":[OSD([subQ1,subQ0])]}),makeQuery(id+"F2.opExtrude","SWEPT_EDGE",EDGE,{"disambiguationData":[OSD([subQ1,subQ0])]})]});}
            var Q3;
            {var subQ0=sQuery(id+"F0.wireOp",EDGE,"E11.MirrorCS");var subQ1=sQuery(id+"F0.wireOp",EDGE,"E4.MirrorCS");Q3=makeQuery(id+"F2.boolean.opBoolean","MERGE",EDGE,{"derivedFrom":[makeQuery(id+"F1.opExtrude","SWEPT_EDGE",EDGE,{"disambiguationData":[OSD([subQ1,subQ0])]}),makeQuery(id+"F2.opExtrude","SWEPT_EDGE",EDGE,{"disambiguationData":[OSD([subQ1,subQ0])]})]});}
            var Q4;
            Q4=makeQuery(id+"F1.opExtrude","SWEPT_EDGE",EDGE,{"disambiguationData":[OSD([sQuery(id+"F0.wireOp",EDGE,"E19"),sQuery(id+"F0.wireOp",EDGE,"E21")])]});
            fillet(context, id + "F29", {"entities" : qUnion([Q0, Q1, Q2, Q3, Q4]), "radius" : 2 * mm, "tangentPropagation" : true, "allowEdgeOverflow" : false});
        }
        {
            var Q0;
            {var subQ0=sQuery(id+"F0.wireOp",EDGE,"E44");var subQ1=sQuery(id+"F0.wireOp",EDGE,"E45");var subQ2=sQuery(id+"F0.wireOp",EDGE,"E37");Q0=makeQuery(id+"F24.opFillet","BLEND_EDGE",EDGE,{"disambiguationData":[OD(1.0)],"blendedFrom":[makeQuery(id+"F23.boolean.opBoolean","MERGE",EDGE,{"derivedFrom":[makeQuery(id+"F14.opExtrude","SWEPT_EDGE",EDGE,{"disambiguationData":[OSD([subQ2,subQ1])]}),makeQuery(id+"F23.opExtrude","SWEPT_EDGE",EDGE,{"disambiguationData":[OSD([subQ2,subQ1])]})]}),makeQuery(id+"F23.boolean.opBoolean","MERGE",FACE,{"derivedFrom":[makeQuery(id+"F14.opExtrude","SWEPT_FACE",FACE,{"disambiguationData":[OSD([subQ0])]}),makeQuery(id+"F23.opExtrude","SWEPT_FACE",FACE,{"disambiguationData":[OSD([subQ0])]})]})],"blendedInto":[makeQuery(id+"F23.boolean.opBoolean","MERGE",FACE,{"derivedFrom":[makeQuery(id+"F14.opExtrude","SWEPT_FACE",FACE,{"disambiguationData":[OSD([subQ0])]}),makeQuery(id+"F23.opExtrude","SWEPT_FACE",FACE,{"disambiguationData":[OSD([subQ0])]})]})]});}
            var Q1;
            {var subQ0=sQuery(id+"F0.wireOp",EDGE,"E44");var subQ1=sQuery(id+"F0.wireOp",EDGE,"E45");var subQ2=sQuery(id+"F0.wireOp",EDGE,"E37");Q1=makeQuery(id+"F24.opFillet","BLEND_EDGE",EDGE,{"disambiguationData":[OD(0.0)],"blendedFrom":[makeQuery(id+"F23.boolean.opBoolean","MERGE",EDGE,{"derivedFrom":[makeQuery(id+"F14.opExtrude","SWEPT_EDGE",EDGE,{"disambiguationData":[OSD([subQ2,subQ1])]}),makeQuery(id+"F23.opExtrude","SWEPT_EDGE",EDGE,{"disambiguationData":[OSD([subQ2,subQ1])]})]}),makeQuery(id+"F23.boolean.opBoolean","MERGE",FACE,{"derivedFrom":[makeQuery(id+"F14.opExtrude","SWEPT_FACE",FACE,{"disambiguationData":[OSD([subQ0])]}),makeQuery(id+"F23.opExtrude","SWEPT_FACE",FACE,{"disambiguationData":[OSD([subQ0])]})]})],"blendedInto":[makeQuery(id+"F23.boolean.opBoolean","MERGE",FACE,{"derivedFrom":[makeQuery(id+"F14.opExtrude","SWEPT_FACE",FACE,{"disambiguationData":[OSD([subQ0])]}),makeQuery(id+"F23.opExtrude","SWEPT_FACE",FACE,{"disambiguationData":[OSD([subQ0])]})]})]});}
            var Q2;
            {var subQ0=sQuery(id+"F0.wireOp",EDGE,"E46");var subQ1=sQuery(id+"F0.wireOp",EDGE,"E44");Q2=makeQuery(id+"F23.boolean.opBoolean","MERGE",EDGE,{"derivedFrom":[makeQuery(id+"F14.opExtrude","SWEPT_EDGE",EDGE,{"disambiguationData":[OSD([subQ1,subQ0])]}),makeQuery(id+"F23.opExtrude","SWEPT_EDGE",EDGE,{"disambiguationData":[OSD([subQ1,subQ0])]})]});}
            fillet(context, id + "F30", {"entities" : qUnion([Q0, Q1, Q2]), "radius" : 1 * mm, "tangentPropagation" : true, "allowEdgeOverflow" : false});
        }
        {
            var Q0;
            {var subQ0=sQuery(id+"F0.wireOp",EDGE,"E12.MirrorCS");Q0=makeQuery(id+"F16.boolean.opBoolean","MERGE",FACE,{"derivedFrom":[makeQuery(id+"F3.boolean.opBoolean","MERGE",FACE,{"derivedFrom":[makeQuery(id+"F2.boolean.opBoolean","MERGE",FACE,{"derivedFrom":[makeQuery(id+"F1.opExtrude","SWEPT_FACE",FACE,{"disambiguationData":[OSD([subQ0])]}),makeQuery(id+"F2.opExtrude","SWEPT_FACE",FACE,{"disambiguationData":[OSD([subQ0])]})]}),makeQuery(id+"F3.opExtrude","SWEPT_FACE",FACE,{"disambiguationData":[OSD([subQ0])]})]}),makeQuery(id+"F16.opExtrude","SWEPT_FACE",FACE,{"disambiguationData":[OSD([sQuery(id+"F4.wireOp",EDGE,"E55.top")])]})]});}
            extrude(context, id + "F31", {"entities" : qUnion([Q0]), "operationType" : NewBodyOperationType.ADD, "depth" : 3 * mm});
        }
        {
            var Q0;
            Q0=makeQuery(id+"F31.opExtrude","CAP_FACE",FACE,{"disambiguationData":[OSD([sQuery(id+"F0.wireOp",EDGE,"E12.MirrorCS"),sQuery(id+"F4.wireOp",EDGE,"E55.top")])],"isStart":false});
            var sketch = newSketch(context, id + "F32", { "sketchPlane" : qUnion([Q0])});
            skCircle(sketch, "E64.cCircle", {"center": v(19.98, 2.5) * mm, "radius": 8.75 * mm, "construction": true});
            skLineSegment(sketch, "E64.0", {"start": v(11.23, -2.55) * mm, "end": v(11.23, 7.55) * mm});
            skLineSegment(sketch, "E64.1", {"start": v(11.23, 7.55) * mm, "end": v(19.98, 12.6) * mm});
            skLineSegment(sketch, "E64.2", {"start": v(19.98, 12.6) * mm, "end": v(28.73, 7.55) * mm});
            skLineSegment(sketch, "E64.3", {"start": v(28.73, 7.55) * mm, "end": v(28.73, -2.55) * mm});
            skLineSegment(sketch, "E64.4", {"start": v(28.73, -2.55) * mm, "end": v(19.98, -7.6) * mm});
            skLineSegment(sketch, "E64.5", {"start": v(19.98, -7.6) * mm, "end": v(11.23, -2.55) * mm});
            skPoint(sketch, "E64.0.midPoint", {"position": v(11.23, 2.5) * mm});
            skSolve(sketch);
        }
        {
            var Q0;
            {var subQ5=sQuery(id+"F32.wireOp",EDGE,"E64.1");Q0=makeQuery(id+"F32.imprint","IMPRINT",FACE,{"disambiguationData":[TD([[makeQuery(id+"F32.imprint","IMPRINT",EDGE,{"derivedFrom":subQ5}),-1.0]])]});}
            extrude(context, id + "F33", {"entities" : qUnion([Q0]), "operationType" : NewBodyOperationType.REMOVE, "oppositeDirection" : true, "depth" : 5.5 * mm});
        }
    });
